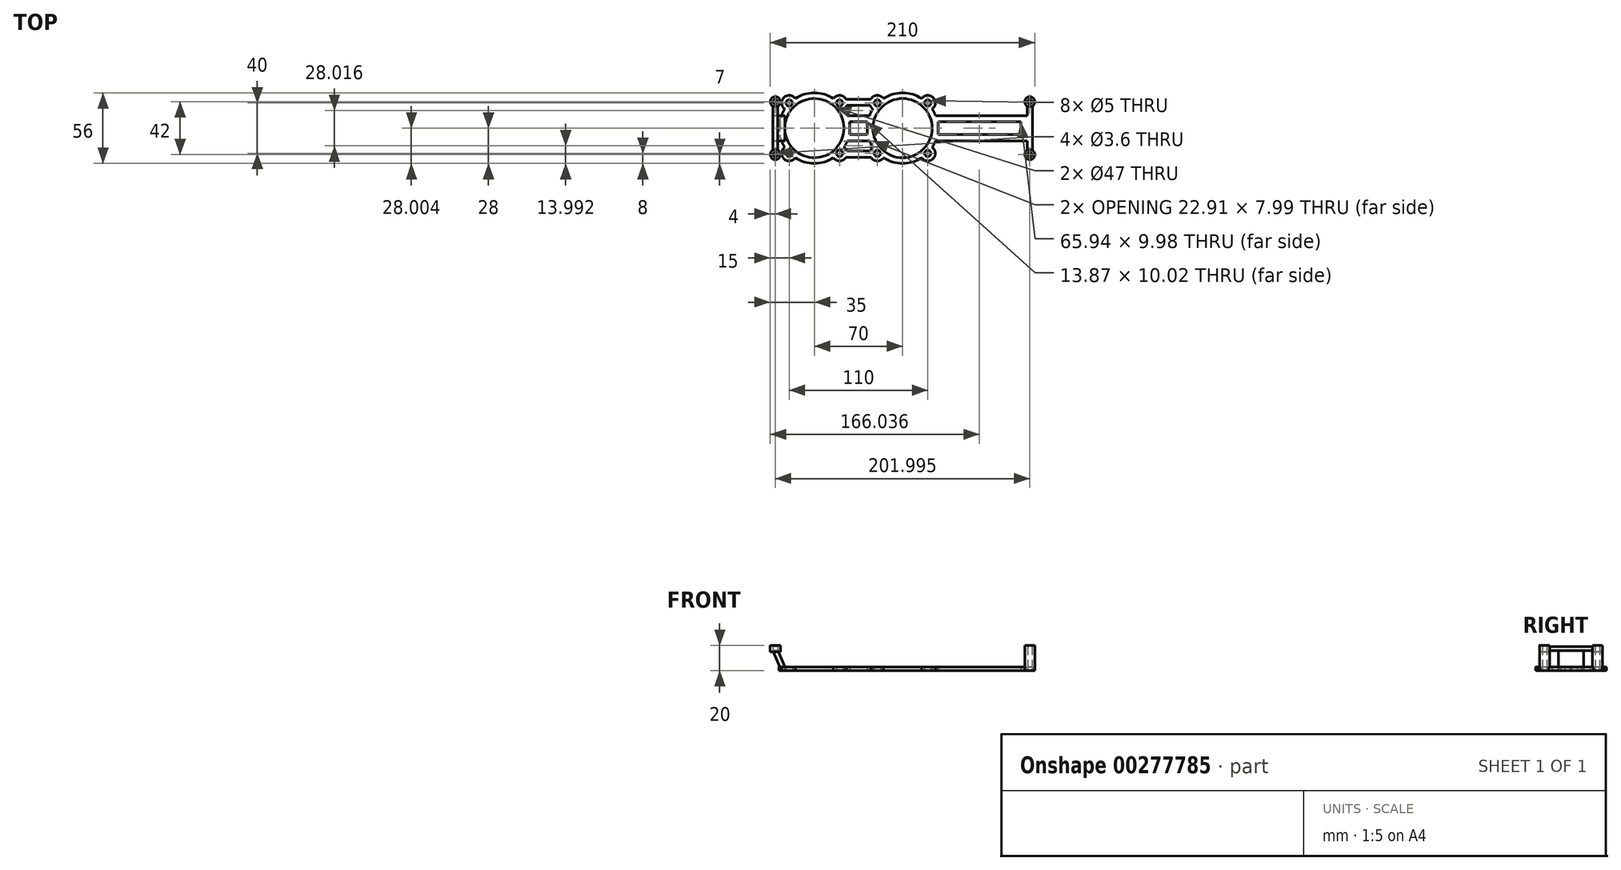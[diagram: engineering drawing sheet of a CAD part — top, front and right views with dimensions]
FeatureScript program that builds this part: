
annotation { "Feature Type Name" : "Feature", "Feature Type Description" : "" }
export const myFeature = defineFeature(function(context is Context, id is Id, definition is map)
    precondition{}
    {
        {
            var Q0;
            Q0=qCreatedBy(makeId("Top.planeOp"),FACE);
            var sketch = newSketch(context, id + "F0", { "sketchPlane" : qUnion([Q0])});
            skCircle(sketch, "E0", {"center": v(0, 0) * mm, "radius": 23.5 * mm});
            skArc(sketch, "E1.0", {"start": v(15.16, 23.54) * mm, "mid": v(0, 28) * mm, "end": v(-15.16, 23.54) * mm});
            skCircle(sketch, "E2", {"center": v(-20, 20) * mm, "radius": 2.5 * mm});
            skCircle(sketch, "E3", {"center": v(20, 20) * mm, "radius": 2.5 * mm});
            skCircle(sketch, "E4", {"center": v(20, -20) * mm, "radius": 2.5 * mm});
            skCircle(sketch, "E5", {"center": v(-20, -20) * mm, "radius": 2.5 * mm});
            skArc(sketch, "E6.0", {"start": v(23.54, 15.16) * mm, "mid": v(24.24, 24.24) * mm, "end": v(15.16, 23.54) * mm});
            skArc(sketch, "E7.0", {"start": v(-15.16, 23.54) * mm, "mid": v(-20.32, 26) * mm, "end": v(-25.2, 23) * mm});
            skArc(sketch, "E8.0", {"start": v(-23.54, -15.16) * mm, "mid": v(-24.82, -16.42) * mm, "end": v(-25.66, -18) * mm});
            skArc(sketch, "E9.0", {"start": v(15.16, -23.54) * mm, "mid": v(24.24, -24.24) * mm, "end": v(23.54, -15.16) * mm});
            skCircle(sketch, "E10", {"center": v(-70, 0) * mm, "radius": 23.5 * mm});
            skArc(sketch, "E11.0", {"start": v(-43.85, 10.01) * mm, "mid": v(-45.02, 12.65) * mm, "end": v(-46.46, 15.16) * mm});
            skCircle(sketch, "E12", {"center": v(-90, 20) * mm, "radius": 2.5 * mm});
            skCircle(sketch, "E13", {"center": v(-50, 20) * mm, "radius": 2.5 * mm});
            skCircle(sketch, "E14", {"center": v(-50, -20) * mm, "radius": 2.5 * mm});
            skCircle(sketch, "E15", {"center": v(-90, -20) * mm, "radius": 2.5 * mm});
            skArc(sketch, "E16.0", {"start": v(-44.8, 23) * mm, "mid": v(-49.68, 26) * mm, "end": v(-54.84, 23.54) * mm});
            skArc(sketch, "E17.0", {"start": v(-85.16, 23.54) * mm, "mid": v(-94.24, 24.24) * mm, "end": v(-93.54, 15.16) * mm});
            skArc(sketch, "E18.0", {"start": v(-93.54, -15.16) * mm, "mid": v(-94.24, -24.24) * mm, "end": v(-85.16, -23.54) * mm});
            skArc(sketch, "E19.0", {"start": v(-44.34, -18) * mm, "mid": v(-45.18, -16.42) * mm, "end": v(-46.46, -15.16) * mm});
            skLineSegment(sketch, "E20", {"start": v(-70, -32.38) * mm, "end": v(-70, 0) * mm, "construction": true});
            skLineSegment(sketch, "E21", {"start": v(-70, 0) * mm, "end": v(-119.07, 0) * mm, "construction": true});
            skLineSegment(sketch, "E22", {"start": v(-44.8, 23) * mm, "end": v(-25.2, 23) * mm});
            skLineSegment(sketch, "E23.0", {"start": v(-44.34, 18) * mm, "end": v(-25.66, 18) * mm});
            skLineSegment(sketch, "E24", {"start": v(-43.85, 10.01) * mm, "end": v(-26.15, 10.01) * mm});
            skLineSegment(sketch, "E25.0", {"start": v(-41.94, 5.01) * mm, "end": v(-28.06, 5.01) * mm});
            skLineSegment(sketch, "E26.MirrorCS", {"start": v(-41.94, -5.01) * mm, "end": v(-28.06, -5.01) * mm});
            skLineSegment(sketch, "E27.MirrorCS", {"start": v(-43.85, -10.01) * mm, "end": v(-26.15, -10.01) * mm});
            skLineSegment(sketch, "E28.MirrorCS", {"start": v(-44.8, -23) * mm, "end": v(-25.2, -23) * mm});
            skLineSegment(sketch, "E29.MirrorCS", {"start": v(-44.34, -18) * mm, "end": v(-25.66, -18) * mm});
            skLineSegment(sketch, "E30.bottom", {"start": v(26.16, 10) * mm, "end": v(99, 10) * mm});
            skLineSegment(sketch, "E30.top", {"start": v(26.16, -9.99) * mm, "end": v(99, -9.99) * mm});
            skLineSegment(sketch, "E30.right", {"start": v(103, 10) * mm, "end": v(103, -9.99) * mm});
            skLineSegment(sketch, "E31.0", {"start": v(28.07, 5) * mm, "end": v(94, 5) * mm});
            skLineSegment(sketch, "E32.0", {"start": v(94, 5) * mm, "end": v(94, -4.99) * mm});
            skArc(sketch, "E33.trimOffspring", {"start": v(-23.54, 15.16) * mm, "mid": v(-24.98, 12.65) * mm, "end": v(-26.15, 10.01) * mm});
            skArc(sketch, "E34.trimOffspring", {"start": v(23.54, -15.16) * mm, "mid": v(24.98, -12.64) * mm, "end": v(26.16, -9.99) * mm});
            skArc(sketch, "E35.trimOffspring", {"start": v(-15.16, -23.54) * mm, "mid": v(0, -28) * mm, "end": v(15.16, -23.54) * mm});
            skPoint(sketch, "E36.orphan", {"position": v(-25.2, -18) * mm});
            skArc(sketch, "E37.trimOffspring", {"start": v(-25.2, -23) * mm, "mid": v(-20.32, -26) * mm, "end": v(-15.16, -23.54) * mm});
            skPoint(sketch, "E38.orphan", {"position": v(-25.2, 18) * mm});
            skArc(sketch, "E39.trimOffspring", {"start": v(-25.66, 18) * mm, "mid": v(-24.82, 16.42) * mm, "end": v(-23.54, 15.16) * mm});
            skLineSegment(sketch, "E40", {"start": v(-28.06, 5.01) * mm, "end": v(-28.06, -5.01) * mm});
            skLineSegment(sketch, "E41", {"start": v(-41.94, 5.01) * mm, "end": v(-41.94, -5.01) * mm});
            skPoint(sketch, "E42.orphan", {"position": v(-26.15, 5.01) * mm});
            skArc(sketch, "E43.trimOffspring", {"start": v(-26.15, -10.01) * mm, "mid": v(-24.98, -12.65) * mm, "end": v(-23.54, -15.16) * mm});
            skPoint(sketch, "E44.orphan", {"position": v(-43.85, 5.01) * mm});
            skPoint(sketch, "E45.orphan", {"position": v(-26.15, -5.01) * mm});
            skPoint(sketch, "E46.orphan", {"position": v(-43.85, -5.01) * mm});
            skPoint(sketch, "E47.orphan", {"position": v(-44.8, 18) * mm});
            skPoint(sketch, "E48.orphan", {"position": v(-44.8, -18) * mm});
            skArc(sketch, "E49.trimOffspring", {"start": v(-54.84, 23.54) * mm, "mid": v(-70, 28) * mm, "end": v(-85.16, 23.54) * mm});
            skArc(sketch, "E50.trimOffspring", {"start": v(-46.46, 15.16) * mm, "mid": v(-45.18, 16.42) * mm, "end": v(-44.34, 18) * mm});
            skArc(sketch, "E51.trimOffspring", {"start": v(-93.54, 15.16) * mm, "mid": v(-98, 0) * mm, "end": v(-93.54, -15.16) * mm});
            skArc(sketch, "E52.trimOffspring", {"start": v(-85.16, -23.54) * mm, "mid": v(-70, -28) * mm, "end": v(-54.84, -23.54) * mm});
            skArc(sketch, "E53.trimOffspring", {"start": v(-46.46, -15.16) * mm, "mid": v(-45.02, -12.65) * mm, "end": v(-43.85, -10.01) * mm});
            skArc(sketch, "E54.trimOffspring", {"start": v(-54.84, -23.54) * mm, "mid": v(-49.68, -26) * mm, "end": v(-44.8, -23) * mm});
            skLineSegment(sketch, "E55", {"start": v(28.07, 5) * mm, "end": v(28.07, -4.99) * mm});
            skLineSegment(sketch, "E56.trimOffspring", {"start": v(28.07, -4.99) * mm, "end": v(94, -4.99) * mm});
            skArc(sketch, "E57.trimOffspring", {"start": v(26.16, 10) * mm, "mid": v(24.98, 12.64) * mm, "end": v(23.54, 15.16) * mm});
            skLineSegment(sketch, "E58", {"start": v(-70, 0) * mm, "end": v(-70, 39.86) * mm, "construction": true});
            skLineSegment(sketch, "E59", {"start": v(99, 10) * mm, "end": v(99, 17.53) * mm});
            skLineSegment(sketch, "E60", {"start": v(103, 10) * mm, "end": v(103, 17.54) * mm});
            skLineSegment(sketch, "E61", {"start": v(103, 17.54) * mm, "end": v(99, 17.53) * mm});
            skLineSegment(sketch, "E62", {"start": v(99, -9.99) * mm, "end": v(99, -17.55) * mm});
            skLineSegment(sketch, "E63", {"start": v(103, -9.99) * mm, "end": v(103, -17.54) * mm});
            skLineSegment(sketch, "E64", {"start": v(103, -17.54) * mm, "end": v(99, -17.55) * mm});
            skSolve(sketch);
        }
        {
            var Q0;
            Q0=qSketchRegion(id+"F0",true);
            extrude(context, id + "F1", {"entities" : qUnion([Q0]), "depth" : 3 * mm});
        }
        {
            var Q0;
            Q0=qCreatedBy(makeId("Top.planeOp"),FACE);
            var sketch = newSketch(context, id + "F2", { "sketchPlane" : qUnion([Q0])});
            skCircle(sketch, "E65", {"center": v(101, 21) * mm, "radius": 1.8 * mm});
            skPoint(sketch, "E65.first.point", {"position": v(100.04, 22.52) * mm});
            skPoint(sketch, "E65.second.point", {"position": v(102.63, 21.76) * mm});
            skPoint(sketch, "E65.third.point", {"position": v(101, 19.2) * mm});
            skCircle(sketch, "E66.0", {"center": v(101, 21) * mm, "radius": 4 * mm});
            skCircle(sketch, "E67.MirrorC", {"center": v(101, -21) * mm, "radius": 1.8 * mm});
            skCircle(sketch, "E68.0", {"center": v(101, -21) * mm, "radius": 4 * mm});
            skSolve(sketch);
        }
        {
            var Q0;
            Q0=qSketchRegion(id+"F2",true);
            extrude(context, id + "F3", {"entities" : qUnion([Q0]), "operationType" : NewBodyOperationType.ADD, "depth" : 20 * mm});
        }
        {
            var Q0;
            Q0=qCreatedBy(makeId("Front.planeOp"),FACE);
            var sketch = newSketch(context, id + "F4", { "sketchPlane" : qUnion([Q0])});
            skLineSegment(sketch, "E69.bottom", {"start": v(-96.08, 0) * mm, "end": v(-93.5, 0) * mm});
            skLineSegment(sketch, "E69.top", {"start": v(-102.88, 16) * mm, "end": v(-99, 16) * mm});
            skLineSegment(sketch, "E69.left", {"start": v(-96.08, 0) * mm, "end": v(-102.88, 16) * mm});
            skLineSegment(sketch, "E69.right", {"start": v(-93.47, 2.98) * mm, "end": v(-99, 16) * mm});
            skLineSegment(sketch, "E70", {"start": v(-93.47, 2.98) * mm, "end": v(-93.5, 0) * mm});
            skSolve(sketch);
        }
        {
            var Q0;
            Q0 = qSketchRegion(id + "F4", true);
            extrude(context, id + "F5", {"entities" : qUnion([Q0]), "operationType" : NewBodyOperationType.ADD, "depth" : 10 * mm, "hasSecondDirection" : true, "secondDirectionOppositeDirection" : true, "secondDirectionDepth" : 10 * mm});
        }
        {
            var Q0;
            Q0=makeQuery(id+"F5.opExtrude","SWEPT_FACE",FACE,{"disambiguationData":[OSD([sQuery(id+"F4.wireOp",EDGE,"E69.top")])]});
            var sketch = newSketch(context, id + "F6", { "sketchPlane" : qUnion([Q0])});
            skLineSegment(sketch, "E71.bottom", {"start": v(-102.9, 18) * mm, "end": v(-99, 18) * mm});
            skLineSegment(sketch, "E71.top", {"start": v(-102.9, -18) * mm, "end": v(-99, -18) * mm});
            skLineSegment(sketch, "E71.left", {"start": v(-102.9, 18) * mm, "end": v(-102.9, -18) * mm});
            skLineSegment(sketch, "E71.right", {"start": v(-99, 18) * mm, "end": v(-99, -18) * mm});
            skSolve(sketch);
        }
        {
            var Q0;
            Q0 = qSketchRegion(id + "F6", true);
            extrude(context, id + "F7", {"entities" : qUnion([Q0]), "operationType" : NewBodyOperationType.ADD, "depth" : 3 * mm});
        }
        {
            var Q0;
            Q0=makeQuery(id+"F7.opExtrude","CAP_FACE",FACE,{"disambiguationData":[OSD([sQuery(id+"F6.wireOp",EDGE,"E71.bottom"),sQuery(id+"F6.wireOp",EDGE,"E71.top"),sQuery(id+"F6.wireOp",EDGE,"E71.left"),sQuery(id+"F6.wireOp",EDGE,"E71.right")])],"isStart":false});
            var sketch = newSketch(context, id + "F8", { "sketchPlane" : qUnion([Q0])});
            skCircle(sketch, "E72", {"center": v(-101, 21) * mm, "radius": 1.8 * mm});
            skCircle(sketch, "E73.0", {"center": v(-101, 21) * mm, "radius": 4 * mm});
            skCircle(sketch, "E74.MirrorC", {"center": v(-101, -21) * mm, "radius": 4 * mm});
            skCircle(sketch, "E75.MirrorC", {"center": v(-101, -21) * mm, "radius": 1.8 * mm});
            skSolve(sketch);
        }
        {
            var Q0;
            Q0 = qSketchRegion(id + "F8", true);
            extrude(context, id + "F9", {"entities" : qUnion([Q0]), "operationType" : NewBodyOperationType.ADD, "depth" : 1 * mm, "hasSecondDirection" : true, "secondDirectionOppositeDirection" : true, "secondDirectionDepth" : 4 * mm});
        }
    });
